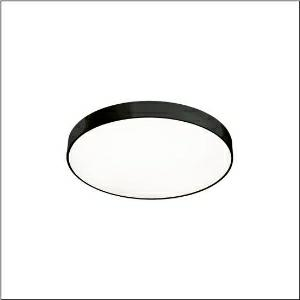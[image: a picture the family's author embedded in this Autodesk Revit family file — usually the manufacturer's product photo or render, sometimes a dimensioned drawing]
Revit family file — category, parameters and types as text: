
# Revit family: round_21_m_51mr36fm8321b
name_source: partatom
category: Lighting Fixtures
units: mm (PartAtom-declared; Revit-internal decimal feet)

## family parameters
Cut with Voids When Loaded = No
Host = Face
Light Source = No
Part Type = Normal
Room Calculation Point = No
Round Connector Dimension = Use Diameter
Shared = No

## types (1)
- --- (1 x LED, 8540 lm, 62.6 W, 3000K)
    Apparent Load = 63 VA
    CIE Flux Codes = 49 80 96 100 100
    Color Rendering = 80
    Color Temperature = 3000K
    Default Elevation = 1800 mm
    Description = Round 21 M, wall and ceiling luminaire, primary optical cover: cover, of PMMA, opal, light emission: direct distribution, primary light characteristic: symmetric, installation type: surface-mounted, suspended mounting, LED, rated luminous flux: 7.700lm, luminous efficacy: 127lm/W, light colour: 830, colour temperature: 3000K, control gear: ON/OFF Multilumen, with terminal, 3-pole, mains connection: 230V, AC, 50/60Hz, rated input power: 61W, housing, of aluminium, coated, black, diameter: 600mm, height: 62mm, protection rating (complete): IP40, insulation class (complete): insulation class I (protective earthing), certification: CE, impact resistance: IK04, permissible operating ambient temperature: -10..+35°C, packaging unit: 1 piece
    Height = 87 mm
    Lamp = 1 x LED
    Lamp Light Flux = 8540 lm
    Lamp Power = 62.6 W
    Lamp count = 1
    Length = 600 mm
    Luminous efficacy = 136 lm/W
    Manufacturer = Siteco
    ModVariant = No
    Model = 51MR36FM8321B
    Mounting Place = Ceiling
    Mounting Type = Surface mounted
    Number of Poles = 1
    OnlyDefault = Yes
    Power Factor = 1
    Product Name = Round 21 M
    Product group = wall and ceiling luminaire
    ProductGroupID = 304
    Protection Class = Protection class I
    Protection Degree = IP 40
    RLX_Detail_Level = 1
    RLX_Emergency_Light_Flux = 0 lm
    RLX_Emergency_Type = 0
    RLX_Emergency_Type_DB = No
    RlxData = <blob elided: 20373 chars, md5=20a59a44>
    Socket = socket
    Standby Power = 0 W
    System Light Flux = 8540 lm
    System Power = 63 W
    Type Comments = factory setting: luminous flux: 100 % | (ON | ON | ON | ON) | 700 mA
    Type Image = l_1258332.jpg
    URL = http://relux.com
    VarID = @adj_032814
    Voltage = 0 V
    Weight = 0.00 kg
    Width = 0 mm  [stored 0 ft]

note: [stored X ft] marks values corroborated as IEEE doubles in the binary element streams (Revit-internal decimal feet)

## geometry (parser evidence)
native form markers: Blend x4, Sweep x9
no freeform markers — native parametric forms only
